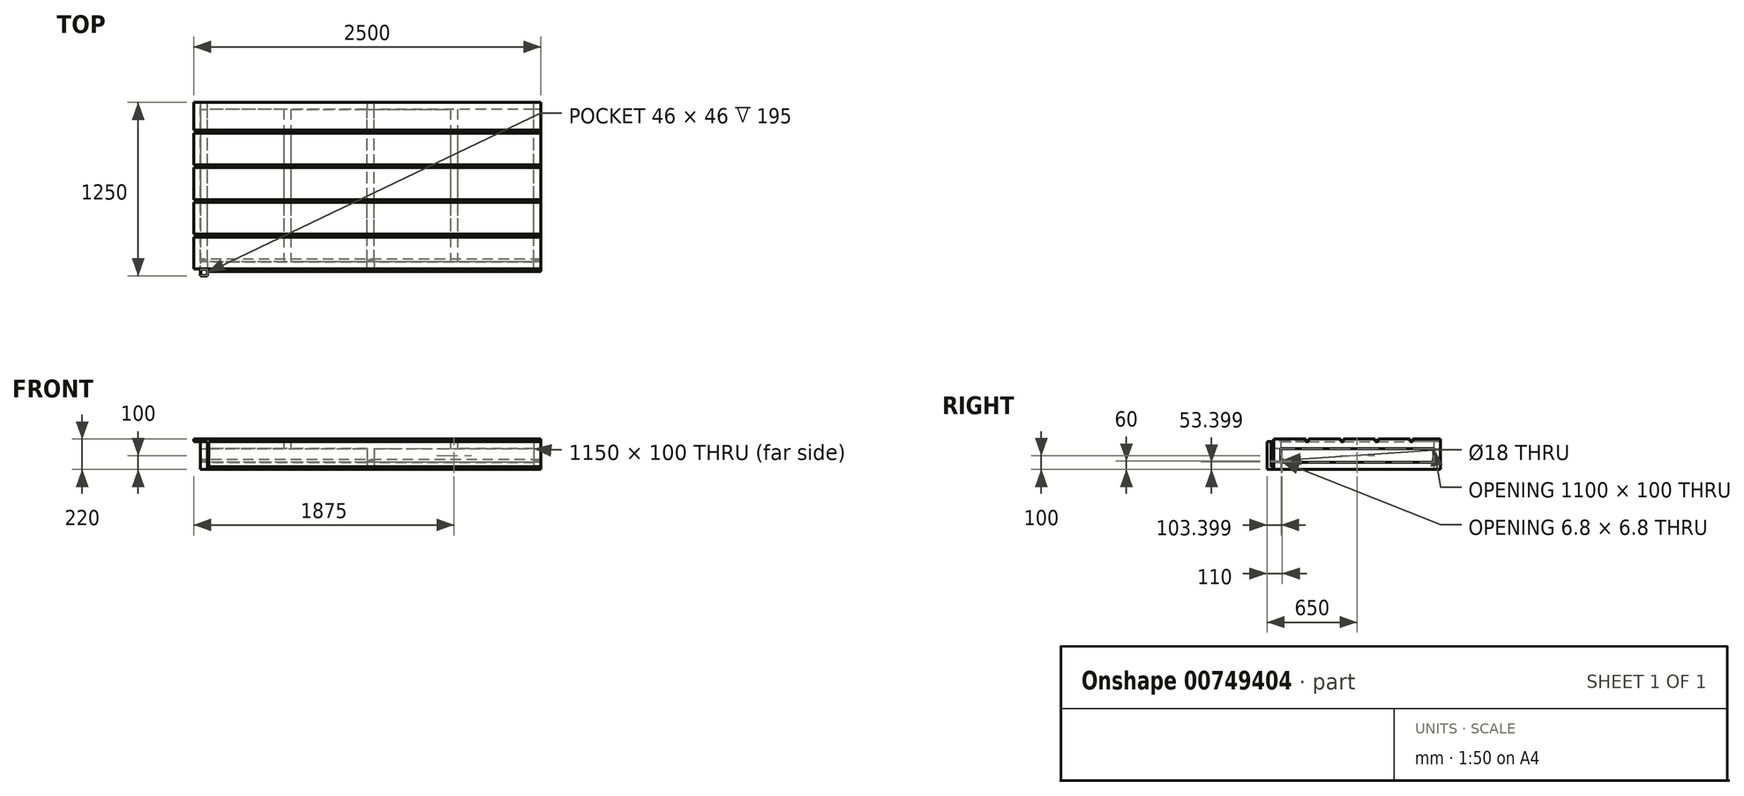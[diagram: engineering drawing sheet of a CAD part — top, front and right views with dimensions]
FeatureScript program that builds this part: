
annotation { "Feature Type Name" : "Feature", "Feature Type Description" : "" }
export const myFeature = defineFeature(function(context is Context, id is Id, definition is map)
    precondition{}
    {
        {
            var Q0;
            Q0=qCreatedBy(makeId("Top.planeOp"),FACE);
            var sketch = newSketch(context, id + "F0", { "sketchPlane" : qUnion([Q0])});
            skLineSegment(sketch, "E0.bottom", {"start": v(1225, -600) * mm, "end": v(-1225, -600) * mm});
            skLineSegment(sketch, "E0.top", {"start": v(1225, 600) * mm, "end": v(-1225, 600) * mm});
            skLineSegment(sketch, "E0.left", {"start": v(1225, -600) * mm, "end": v(1225, 600) * mm});
            skLineSegment(sketch, "E0.right", {"start": v(-1225, -600) * mm, "end": v(-1225, 600) * mm});
            skPoint(sketch, "E0.middle", {"position": v(0, 0) * mm});
            skLineSegment(sketch, "E1.0", {"start": v(1225, 550) * mm, "end": v(-1225, 550) * mm});
            skLineSegment(sketch, "E2.0", {"start": v(1227.5, -600) * mm, "end": v(1227.5, 600) * mm});
            skLineSegment(sketch, "E3.0", {"start": v(1175, -600) * mm, "end": v(1175, 600) * mm});
            skLineSegment(sketch, "E4.0", {"start": v(1225, -550) * mm, "end": v(-1225, -550) * mm});
            skLineSegment(sketch, "E5.0", {"start": v(-1175, -600) * mm, "end": v(-1175, 600) * mm});
            skLineSegment(sketch, "E6", {"start": v(0, 0) * mm, "end": v(0, 550) * mm});
            skLineSegment(sketch, "E7", {"start": v(0, 0) * mm, "end": v(0, -550) * mm});
            skLineSegment(sketch, "E8.0", {"start": v(25, 0) * mm, "end": v(25, 550) * mm});
            skLineSegment(sketch, "E9.0", {"start": v(-25, 0) * mm, "end": v(-25, 550) * mm});
            skLineSegment(sketch, "E10.0", {"start": v(-25, 0) * mm, "end": v(-25, -550) * mm});
            skLineSegment(sketch, "E11.0", {"start": v(25, 0) * mm, "end": v(25, -550) * mm});
            skSolve(sketch);
        }
        {
            var Q0;
            Q0=qSketchRegion(id+"F0",true);
            var Q1;
            {var subQ1=sQuery(id+"F0.wireOp",EDGE,"E6");Q1=makeQuery(id+"F0.imprint","IMPRINT",FACE,{"disambiguationData":[TD([[makeQuery(id+"F0.imprint","IMPRINT",EDGE,{"derivedFrom":subQ1}),-1.0]])]});}
            var Q2;
            {var subQ3=sQuery(id+"F0.wireOp",EDGE,"E6");Q2=makeQuery(id+"F0.imprint","IMPRINT",FACE,{"disambiguationData":[TD([[makeQuery(id+"F0.imprint","IMPRINT",EDGE,{"derivedFrom":subQ3}),1.0]])]});}
            extrude(context, id + "F1", {"entities" : qUnion([Q0, Q1, Q2]), "depth" : 50 * mm, "offsetDistance" : 25 * mm});
        }
        {
            var Q0;
            Q0=makeQuery(id+"F1.opExtrude","CAP_FACE",FACE,{"disambiguationData":[OSD([sQuery(id+"F0.wireOp",EDGE,"E0.bottom"),sQuery(id+"F0.wireOp",EDGE,"E0.top"),sQuery(id+"F0.wireOp",EDGE,"E0.left"),sQuery(id+"F0.wireOp",EDGE,"E0.right"),sQuery(id+"F0.wireOp",EDGE,"E1.0"),sQuery(id+"F0.wireOp",EDGE,"E3.0"),sQuery(id+"F0.wireOp",EDGE,"E4.0"),sQuery(id+"F0.wireOp",EDGE,"E5.0"),sQuery(id+"F0.wireOp",EDGE,"E8.0"),sQuery(id+"F0.wireOp",EDGE,"E9.0"),sQuery(id+"F0.wireOp",EDGE,"E10.0"),sQuery(id+"F0.wireOp",EDGE,"E11.0")])],"isStart":false});
            var sketch = newSketch(context, id + "F2", { "sketchPlane" : qUnion([Q0])});
            skLineSegment(sketch, "E12", {"start": v(-25, 550) * mm, "end": v(25, 550) * mm});
            skLineSegment(sketch, "E13", {"start": v(25, 550) * mm, "end": v(25, 600) * mm});
            skLineSegment(sketch, "E14", {"start": v(25, 600) * mm, "end": v(-25, 600) * mm});
            skLineSegment(sketch, "E15", {"start": v(-25, 600) * mm, "end": v(-25, 550) * mm});
            skLineSegment(sketch, "E16", {"start": v(-1175, 550) * mm, "end": v(-1175, 600) * mm});
            skLineSegment(sketch, "E17", {"start": v(-1175, 600) * mm, "end": v(-1225, 600) * mm});
            skLineSegment(sketch, "E18", {"start": v(-1225, 600) * mm, "end": v(-1225, 550) * mm});
            skLineSegment(sketch, "E19", {"start": v(-1225, 550) * mm, "end": v(-1175, 550) * mm});
            skLineSegment(sketch, "E20", {"start": v(-1175, -550) * mm, "end": v(-1175, -600) * mm});
            skLineSegment(sketch, "E21", {"start": v(-1175, -600) * mm, "end": v(-1225, -600) * mm});
            skLineSegment(sketch, "E22", {"start": v(-1225, -600) * mm, "end": v(-1225, -550) * mm});
            skLineSegment(sketch, "E23", {"start": v(-1225, -550) * mm, "end": v(-1175, -550) * mm});
            skLineSegment(sketch, "E24", {"start": v(-25, -550) * mm, "end": v(25, -550) * mm});
            skLineSegment(sketch, "E25", {"start": v(25, -550) * mm, "end": v(25, -600) * mm});
            skLineSegment(sketch, "E26", {"start": v(25, -600) * mm, "end": v(-25, -600) * mm});
            skPoint(sketch, "E26.endSnap0", {"position": v(0, -600) * mm});
            skLineSegment(sketch, "E27", {"start": v(-25, -600) * mm, "end": v(-25, -550) * mm});
            skLineSegment(sketch, "E28", {"start": v(1175, -550) * mm, "end": v(1225, -550) * mm});
            skLineSegment(sketch, "E29", {"start": v(1225, -550) * mm, "end": v(1225, -600) * mm});
            skLineSegment(sketch, "E30", {"start": v(1225, -600) * mm, "end": v(1175, -600) * mm});
            skLineSegment(sketch, "E31", {"start": v(1175, -600) * mm, "end": v(1175, -550) * mm});
            skLineSegment(sketch, "E32", {"start": v(1175, 550) * mm, "end": v(1175, 600) * mm});
            skLineSegment(sketch, "E33", {"start": v(1175, 600) * mm, "end": v(1225, 600) * mm});
            skLineSegment(sketch, "E34", {"start": v(1225, 600) * mm, "end": v(1225, 550) * mm});
            skLineSegment(sketch, "E35", {"start": v(1225, 550) * mm, "end": v(1175, 550) * mm});
            skSolve(sketch);
        }
        {
            var Q0;
            Q0=qSketchRegion(id+"F2",true);
            extrude(context, id + "F3", {"entities" : qUnion([Q0]), "operationType" : NewBodyOperationType.ADD, "depth" : 100 * mm, "offsetDistance" : 25 * mm});
        }
        {
            var Q0;
            Q0=makeQuery(id+"F3.opExtrude","CAP_FACE",FACE,{"disambiguationData":[OSD([sQuery(id+"F2.wireOp",EDGE,"E12"),sQuery(id+"F2.wireOp",EDGE,"E13"),sQuery(id+"F2.wireOp",EDGE,"E14"),sQuery(id+"F2.wireOp",EDGE,"E15")])],"isStart":false});
            var sketch = newSketch(context, id + "F4", { "sketchPlane" : qUnion([Q0])});
            skLineSegment(sketch, "E36.bottom", {"start": v(-1225, 600) * mm, "end": v(1225, 600) * mm});
            skLineSegment(sketch, "E36.top", {"start": v(-1225, -600) * mm, "end": v(1225, -600) * mm});
            skLineSegment(sketch, "E36.left", {"start": v(-1225, 600) * mm, "end": v(-1225, -600) * mm});
            skLineSegment(sketch, "E36.right", {"start": v(1225, 600) * mm, "end": v(1225, -600) * mm});
            skLineSegment(sketch, "E37.bottom", {"start": v(1175, -550) * mm, "end": v(-1175, -550) * mm});
            skLineSegment(sketch, "E37.top", {"start": v(1175, 550) * mm, "end": v(-1175, 550) * mm});
            skLineSegment(sketch, "E37.left", {"start": v(1175, -550) * mm, "end": v(1175, 550) * mm});
            skLineSegment(sketch, "E37.right", {"start": v(-1175, -550) * mm, "end": v(-1175, 550) * mm});
            skLineSegment(sketch, "E38.bottom", {"start": v(-25, 550) * mm, "end": v(25, 550) * mm});
            skLineSegment(sketch, "E38.top", {"start": v(-25, -550) * mm, "end": v(25, -550) * mm});
            skLineSegment(sketch, "E38.left", {"start": v(-25, 550) * mm, "end": v(-25, -550) * mm});
            skLineSegment(sketch, "E38.right", {"start": v(25, 550) * mm, "end": v(25, -550) * mm});
            skLineSegment(sketch, "E39", {"start": v(-25, 550) * mm, "end": v(-1175, 550) * mm});
            skLineSegment(sketch, "E40", {"start": v(-600, 550) * mm, "end": v(-600, -550) * mm});
            skLineSegment(sketch, "E41.0", {"start": v(-625, 550) * mm, "end": v(-625, -550) * mm});
            skLineSegment(sketch, "E42.0", {"start": v(-575, 550) * mm, "end": v(-575, -550) * mm});
            skLineSegment(sketch, "E43", {"start": v(25, 550) * mm, "end": v(1175, 550) * mm});
            skLineSegment(sketch, "E44", {"start": v(600, 550) * mm, "end": v(600, -550) * mm});
            skLineSegment(sketch, "E45.0", {"start": v(575, 550) * mm, "end": v(575, -550) * mm});
            skLineSegment(sketch, "E46.0", {"start": v(625, 550) * mm, "end": v(625, -550) * mm});
            skSolve(sketch);
        }
        {
            var Q0;
            Q0=qSketchRegion(id+"F4",true);
            var Q1;
            {var subQ0=sQuery(id+"F4.wireOp",EDGE,"E40");Q1=makeQuery(id+"F4.imprint","IMPRINT",FACE,{"disambiguationData":[TD([[makeQuery(id+"F4.imprint","IMPRINT",EDGE,{"derivedFrom":subQ0}),1.0]])]});}
            var Q2;
            {var subQ0=sQuery(id+"F4.wireOp",EDGE,"E40");Q2=makeQuery(id+"F4.imprint","IMPRINT",FACE,{"disambiguationData":[TD([[makeQuery(id+"F4.imprint","IMPRINT",EDGE,{"derivedFrom":subQ0}),-1.0]])]});}
            var Q3;
            {var subQ0=sQuery(id+"F4.wireOp",EDGE,"E44");Q3=makeQuery(id+"F4.imprint","IMPRINT",FACE,{"disambiguationData":[TD([[makeQuery(id+"F4.imprint","IMPRINT",EDGE,{"derivedFrom":subQ0}),1.0]])]});}
            var Q4;
            {var subQ0=sQuery(id+"F4.wireOp",EDGE,"E44");Q4=makeQuery(id+"F4.imprint","IMPRINT",FACE,{"disambiguationData":[TD([[makeQuery(id+"F4.imprint","IMPRINT",EDGE,{"derivedFrom":subQ0}),-1.0]])]});}
            var Q5;
            Q5=makeQuery(id+"F4.imprint","IMPRINT",FACE,{"disambiguationData":[TD([[makeQuery(id+"F4.imprint","IMPRINT",EDGE,{"derivedFrom":sQuery(id+"F4.wireOp",EDGE,"E38.bottom")}),-1.0]])]});
            extrude(context, id + "F5", {"entities" : qUnion([Q0, Q1, Q2, Q3, Q4, Q5]), "operationType" : NewBodyOperationType.ADD, "depth" : 50 * mm, "offsetDistance" : 25 * mm});
        }
        {
            var Q0;
            Q0=makeQuery(id+"F5.boolean.opBoolean","MERGE",FACE,{"derivedFrom":[makeQuery(id+"F3.boolean.opBoolean","MERGE",FACE,{"derivedFrom":[makeQuery(id+"F1.opExtrude","SWEPT_FACE",FACE,{"disambiguationData":[OSD([sQuery(id+"F0.wireOp",EDGE,"E0.right")])]}),makeQuery(id+"F3.opExtrude","SWEPT_FACE",FACE,{"disambiguationData":[OSD([sQuery(id+"F2.wireOp",EDGE,"E18")])]}),makeQuery(id+"F3.opExtrude","SWEPT_FACE",FACE,{"disambiguationData":[OSD([sQuery(id+"F2.wireOp",EDGE,"E22")])]})]}),makeQuery(id+"F5.opExtrude","SWEPT_FACE",FACE,{"disambiguationData":[OSD([sQuery(id+"F4.wireOp",EDGE,"E36.left")])]})]});
            var sketch = newSketch(context, id + "F6", { "sketchPlane" : qUnion([Q0])});
            skLineSegment(sketch, "E47", {"start": v(550, 50) * mm, "end": v(550, 60) * mm});
            skLineSegment(sketch, "E48", {"start": v(550, 60) * mm, "end": v(540, 60) * mm});
            skCircle(sketch, "E49", {"center": v(540, 60) * mm, "radius": 10.5 * mm});
            skCircle(sketch, "E50", {"center": v(540, 60) * mm, "radius": 9 * mm});
            skSolve(sketch);
        }
        {
            var Q0;
            Q0=qSketchRegion(id+"F6",true);
            extrude(context, id + "F7", {"entities" : qUnion([Q0]), "operationType" : NewBodyOperationType.ADD, "oppositeDirection" : true, "depth" : 2450 * mm, "offsetDistance" : 25 * mm});
        }
        {
            var Q0;
            Q0=makeQuery(id+"F5.boolean.opBoolean","MERGE",FACE,{"derivedFrom":[makeQuery(id+"F3.boolean.opBoolean","MERGE",FACE,{"derivedFrom":[makeQuery(id+"F1.opExtrude","SWEPT_FACE",FACE,{"disambiguationData":[OSD([sQuery(id+"F0.wireOp",EDGE,"E0.bottom")])]}),makeQuery(id+"F3.opExtrude","SWEPT_FACE",FACE,{"disambiguationData":[OSD([sQuery(id+"F2.wireOp",EDGE,"E21")])]}),makeQuery(id+"F3.opExtrude","SWEPT_FACE",FACE,{"disambiguationData":[OSD([sQuery(id+"F2.wireOp",EDGE,"E26")])]}),makeQuery(id+"F3.opExtrude","SWEPT_FACE",FACE,{"disambiguationData":[OSD([sQuery(id+"F2.wireOp",EDGE,"E30")])]})]}),makeQuery(id+"F5.opExtrude","SWEPT_FACE",FACE,{"disambiguationData":[OSD([sQuery(id+"F4.wireOp",EDGE,"E36.top")])]})]});
            var sketch = newSketch(context, id + "F8", { "sketchPlane" : qUnion([Q0])});
            skLineSegment(sketch, "E51.bottom", {"start": v(1225, 200) * mm, "end": v(-1275, 200) * mm});
            skLineSegment(sketch, "E51.top", {"start": v(1225, 20) * mm, "end": v(-1275, 20) * mm});
            skLineSegment(sketch, "E51.left", {"start": v(1225, 200) * mm, "end": v(1225, 20) * mm});
            skLineSegment(sketch, "E51.right", {"start": v(-1275, 200) * mm, "end": v(-1275, 20) * mm});
            skLineSegment(sketch, "E52", {"start": v(-1225, 200) * mm, "end": v(-1275, 200) * mm});
            skSolve(sketch);
        }
        {
            var Q0;
            Q0=qSketchRegion(id+"F8",true);
            extrude(context, id + "F9", {"entities" : qUnion([Q0]), "depth" : 20 * mm, "offsetDistance" : 25 * mm});
        }
        {
            var Q0;
            Q0=makeQuery(id+"F5.opExtrude","CAP_FACE",FACE,{"disambiguationData":[OSD([sQuery(id+"F4.wireOp",EDGE,"E36.bottom"),sQuery(id+"F4.wireOp",EDGE,"E36.top"),sQuery(id+"F4.wireOp",EDGE,"E36.left"),sQuery(id+"F4.wireOp",EDGE,"E36.right"),sQuery(id+"F4.wireOp",EDGE,"E37.bottom"),sQuery(id+"F4.wireOp",EDGE,"E37.left"),sQuery(id+"F4.wireOp",EDGE,"E37.right"),sQuery(id+"F4.wireOp",EDGE,"E38.left"),sQuery(id+"F4.wireOp",EDGE,"E38.right"),sQuery(id+"F4.wireOp",EDGE,"E39"),sQuery(id+"F4.wireOp",EDGE,"E41.0"),sQuery(id+"F4.wireOp",EDGE,"E42.0"),sQuery(id+"F4.wireOp",EDGE,"E43"),sQuery(id+"F4.wireOp",EDGE,"E45.0"),sQuery(id+"F4.wireOp",EDGE,"E46.0")])],"isStart":false});
            var sketch = newSketch(context, id + "F10", { "sketchPlane" : qUnion([Q0])});
            skLineSegment(sketch, "E53.bottom", {"start": v(1225, 600) * mm, "end": v(-1275, 600) * mm});
            skLineSegment(sketch, "E53.top", {"start": v(1225, -600) * mm, "end": v(-1275, -600) * mm});
            skLineSegment(sketch, "E53.left", {"start": v(1225, 600) * mm, "end": v(1225, -600) * mm});
            skLineSegment(sketch, "E53.right", {"start": v(-1275, 600) * mm, "end": v(-1275, -600) * mm});
            skSolve(sketch);
        }
        {
            var Q0;
            Q0=qSketchRegion(id+"F10",true);
            extrude(context, id + "F11", {"entities" : qUnion([Q0]), "depth" : 20 * mm, "offsetDistance" : 25 * mm});
        }
        {
            var Q0;
            Q0=makeQuery(id+"F9.opExtrude","SWEPT_FACE",FACE,{"disambiguationData":[OSD([sQuery(id+"F8.wireOp",EDGE,"E51.right")])]});
            extrude(context, id + "F12", {"entities" : qUnion([Q0]), "operationType" : NewBodyOperationType.REMOVE, "oppositeDirection" : true, "depth" : 110 * mm, "offsetDistance" : 25 * mm});
        }
        {
            var Q0;
            Q0=makeQuery(id+"F1.opExtrude","CAP_FACE",FACE,{"disambiguationData":[OSD([sQuery(id+"F0.wireOp",EDGE,"E0.bottom"),sQuery(id+"F0.wireOp",EDGE,"E0.top"),sQuery(id+"F0.wireOp",EDGE,"E0.left"),sQuery(id+"F0.wireOp",EDGE,"E0.right"),sQuery(id+"F0.wireOp",EDGE,"E1.0"),sQuery(id+"F0.wireOp",EDGE,"E3.0"),sQuery(id+"F0.wireOp",EDGE,"E4.0"),sQuery(id+"F0.wireOp",EDGE,"E5.0"),sQuery(id+"F0.wireOp",EDGE,"E8.0"),sQuery(id+"F0.wireOp",EDGE,"E9.0"),sQuery(id+"F0.wireOp",EDGE,"E10.0"),sQuery(id+"F0.wireOp",EDGE,"E11.0")])],"isStart":true});
            var sketch = newSketch(context, id + "F13", { "sketchPlane" : qUnion([Q0])});
            skLineSegment(sketch, "E54", {"start": v(-1225, 600) * mm, "end": v(-1225, 650) * mm});
            skLineSegment(sketch, "E55.bottom", {"start": v(-1225, 650) * mm, "end": v(-1175, 650) * mm});
            skLineSegment(sketch, "E55.top", {"start": v(-1225, 600) * mm, "end": v(-1175, 600) * mm});
            skLineSegment(sketch, "E55.left", {"start": v(-1225, 650) * mm, "end": v(-1225, 600) * mm});
            skLineSegment(sketch, "E55.right", {"start": v(-1175, 650) * mm, "end": v(-1175, 600) * mm});
            skSolve(sketch);
        }
        {
            var Q0;
            Q0 = qSketchRegion(id + "F13", true);
            extrude(context, id + "F14", {"entities" : qUnion([Q0]), "operationType" : NewBodyOperationType.ADD, "oppositeDirection" : true, "depth" : 5 * mm, "offsetDistance" : 25 * mm});
        }
        {
            var Q0;
            Q0=makeQuery(id+"F14.opExtrude","CAP_FACE",FACE,{"disambiguationData":[OSD([sQuery(id+"F13.wireOp",EDGE,"E55.bottom"),sQuery(id+"F13.wireOp",EDGE,"E55.top"),sQuery(id+"F13.wireOp",EDGE,"E55.left"),sQuery(id+"F13.wireOp",EDGE,"E55.right")])],"isStart":false});
            var sketch = newSketch(context, id + "F15", { "sketchPlane" : qUnion([Q0])});
            skLineSegment(sketch, "E56.bottom", {"start": v(-1225, -600) * mm, "end": v(-1175, -600) * mm});
            skLineSegment(sketch, "E56.top", {"start": v(-1225, -650) * mm, "end": v(-1175, -650) * mm});
            skLineSegment(sketch, "E56.left", {"start": v(-1225, -600) * mm, "end": v(-1225, -650) * mm});
            skLineSegment(sketch, "E56.right", {"start": v(-1175, -600) * mm, "end": v(-1175, -650) * mm});
            skLineSegment(sketch, "E57.bottom", {"start": v(-1225, -600) * mm, "end": v(-1223, -600) * mm});
            skLineSegment(sketch, "E57.top", {"start": v(-1225, -602) * mm, "end": v(-1223, -602) * mm});
            skLineSegment(sketch, "E57.left", {"start": v(-1225, -600) * mm, "end": v(-1225, -602) * mm});
            skLineSegment(sketch, "E57.right", {"start": v(-1223, -600) * mm, "end": v(-1223, -602) * mm});
            skLineSegment(sketch, "E58.bottom", {"start": v(-1223, -602) * mm, "end": v(-1177, -602) * mm});
            skLineSegment(sketch, "E58.top", {"start": v(-1223, -648) * mm, "end": v(-1177, -648) * mm});
            skLineSegment(sketch, "E58.left", {"start": v(-1223, -602) * mm, "end": v(-1223, -648) * mm});
            skLineSegment(sketch, "E58.right", {"start": v(-1177, -602) * mm, "end": v(-1177, -648) * mm});
            skSolve(sketch);
        }
        {
            var Q0;
            Q0 = qSketchRegion(id + "F15", true);
            var Q1;
            Q1=makeQuery(id+"F11.opExtrude","CAP_FACE",FACE,{"disambiguationData":[OSD([sQuery(id+"F10.wireOp",EDGE,"E53.bottom"),sQuery(id+"F10.wireOp",EDGE,"E53.top"),sQuery(id+"F10.wireOp",EDGE,"E53.left"),sQuery(id+"F10.wireOp",EDGE,"E53.right")])],"isStart":true});
            extrude(context, id + "F16", {"entities" : qUnion([Q0]), "operationType" : NewBodyOperationType.ADD, "endBound" : BoundingType.UP_TO_SURFACE, "depth" : 25 * mm, "endBoundEntityFace" : qUnion([Q1]), "offsetDistance" : 25 * mm});
        }
        {
            var Q0;
            Q0=makeQuery(id+"F11.opExtrude","SWEPT_FACE",FACE,{"disambiguationData":[OSD([sQuery(id+"F10.wireOp",EDGE,"E53.right")])]});
            var sketch = newSketch(context, id + "F17", { "sketchPlane" : qUnion([Q0])});
            skLineSegment(sketch, "E59.bottom", {"start": v(600, 200) * mm, "end": v(620.46, 200) * mm});
            skLineSegment(sketch, "E59.top", {"start": v(600, 220) * mm, "end": v(620.46, 220) * mm});
            skLineSegment(sketch, "E59.left", {"start": v(600, 200) * mm, "end": v(600, 220) * mm});
            skLineSegment(sketch, "E59.right", {"start": v(620.46, 200) * mm, "end": v(620.46, 220) * mm});
            skLineSegment(sketch, "E60.1.0.0", {"start": v(350, 220) * mm, "end": v(370.46, 220) * mm});
            skLineSegment(sketch, "E60.1.0.1", {"start": v(370.46, 200) * mm, "end": v(370.46, 220) * mm});
            skLineSegment(sketch, "E60.1.0.2", {"start": v(350, 200) * mm, "end": v(370.46, 200) * mm});
            skLineSegment(sketch, "E60.1.0.3", {"start": v(350, 200) * mm, "end": v(350, 220) * mm});
            skLineSegment(sketch, "E60.2.0.0", {"start": v(100, 220) * mm, "end": v(120.46, 220) * mm});
            skLineSegment(sketch, "E60.2.0.1", {"start": v(120.46, 200) * mm, "end": v(120.46, 220) * mm});
            skLineSegment(sketch, "E60.2.0.2", {"start": v(100, 200) * mm, "end": v(120.46, 200) * mm});
            skLineSegment(sketch, "E60.2.0.3", {"start": v(100, 200) * mm, "end": v(100, 220) * mm});
            skLineSegment(sketch, "E60.3.0.0", {"start": v(-150, 220) * mm, "end": v(-129.54, 220) * mm});
            skLineSegment(sketch, "E60.3.0.1", {"start": v(-129.54, 200) * mm, "end": v(-129.54, 220) * mm});
            skLineSegment(sketch, "E60.3.0.2", {"start": v(-150, 200) * mm, "end": v(-129.54, 200) * mm});
            skLineSegment(sketch, "E60.3.0.3", {"start": v(-150, 200) * mm, "end": v(-150, 220) * mm});
            skLineSegment(sketch, "E60.4.0.0", {"start": v(-400, 220) * mm, "end": v(-379.54, 220) * mm});
            skLineSegment(sketch, "E60.4.0.1", {"start": v(-379.54, 200) * mm, "end": v(-379.54, 220) * mm});
            skLineSegment(sketch, "E60.4.0.2", {"start": v(-400, 200) * mm, "end": v(-379.54, 200) * mm});
            skLineSegment(sketch, "E60.4.0.3", {"start": v(-400, 200) * mm, "end": v(-400, 220) * mm});
            skLineSegment(sketch, "E60.direction1", {"start": v(600, 200) * mm, "end": v(350, 200) * mm, "construction": true});
            skSolve(sketch);
        }
        {
            var Q0;
            Q0 = qSketchRegion(id + "F17", true);
            var Q1;
            Q1=makeQuery(id+"F11.opExtrude","SWEPT_FACE",FACE,{"disambiguationData":[OSD([sQuery(id+"F10.wireOp",EDGE,"E53.left")])]});
            extrude(context, id + "F18", {"entities" : qUnion([Q0]), "operationType" : NewBodyOperationType.REMOVE, "endBound" : BoundingType.UP_TO_SURFACE, "oppositeDirection" : true, "depth" : 25 * mm, "endBoundEntityFace" : qUnion([Q1]), "offsetDistance" : 25 * mm});
        }
    });
